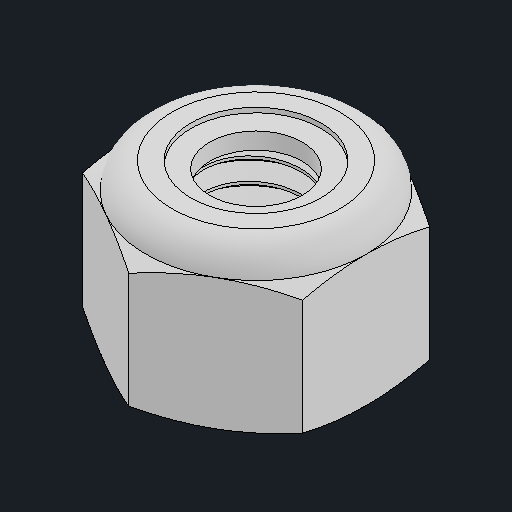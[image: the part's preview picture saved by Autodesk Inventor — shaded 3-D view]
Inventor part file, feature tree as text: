
AUTODESK INVENTOR PART (.ipt)
format: ipt  version: 2024.2 (Build 282272000, 272)  size: 334,336 bytes
history: native  units: mm
features: other x3, revolve x1
ambient origin geometry x8: Origin, YZ Plane, XZ Plane, XY Plane, X Axis, Y Axis, Z Axis, Center Point
bodies: Body1 (feature_tree), Body2 (feature_tree)
feature tree (4):
  other  "솔리드1"
  other  "솔리드2"
  other  "Cut-Revolve4"
  revolve  "Revolve2"  [1 undecoded]
note: 1 required parameter value undecoded (feature->parameter linkage not recoverable at this tier; creation-order binding heuristic only, values carry confidence <= 0.55)
